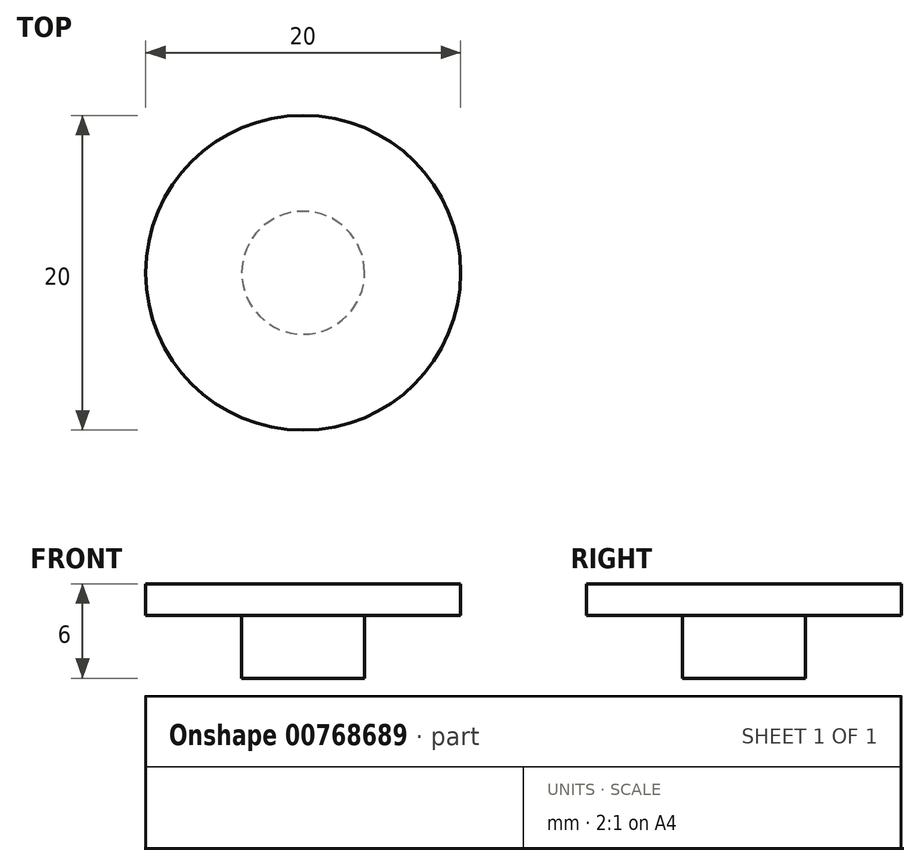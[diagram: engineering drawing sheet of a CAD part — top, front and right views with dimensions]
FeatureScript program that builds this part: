
annotation { "Feature Type Name" : "Feature", "Feature Type Description" : "" }
export const myFeature = defineFeature(function(context is Context, id is Id, definition is map)
    precondition{}
    {
        {
            var Q0;
            Q0=qCreatedBy(makeId("Top.planeOp"),FACE);
            var sketch = newSketch(context, id + "F0", { "sketchPlane" : qUnion([Q0])});
            skCircle(sketch, "E0", {"center": v(0, 0) * mm, "radius": 10 * mm});
            skSolve(sketch);
        }
        {
            var Q0;
            Q0=makeQuery(id+"F0.imprint","IMPRINT",FACE,{"disambiguationData":[TD([[makeQuery(id+"F0.imprint","IMPRINT",EDGE,{"derivedFrom":sQuery(id+"F0.wireOp",EDGE,"E0")}),1.0]])]});
            var sketch = newSketch(context, id + "F1", { "sketchPlane" : qUnion([Q0])});
            skCircle(sketch, "E1", {"center": v(0, 0) * mm, "radius": 3.9 * mm});
            skSolve(sketch);
        }
        {
            var Q0;
            Q0=makeQuery(id+"F0.imprint","IMPRINT",FACE,{"disambiguationData":[TD([[makeQuery(id+"F0.imprint","IMPRINT",EDGE,{"derivedFrom":sQuery(id+"F0.wireOp",EDGE,"E0")}),1.0]])]});
            extrude(context, id + "F2", {"entities" : qUnion([Q0]), "depth" : 2 * mm, "offsetDistance" : 25.4 * mm});
        }
        {
            var Q0;
            Q0=makeQuery(id+"F1.imprint","IMPRINT",FACE,{"disambiguationData":[TD([[makeQuery(id+"F1.imprint","IMPRINT",EDGE,{"derivedFrom":sQuery(id+"F1.wireOp",EDGE,"E1")}),1.0]])]});
            extrude(context, id + "F3", {"entities" : qUnion([Q0]), "operationType" : NewBodyOperationType.ADD, "oppositeDirection" : true, "depth" : 4 * mm, "offsetDistance" : 25.4 * mm});
        }
    });
